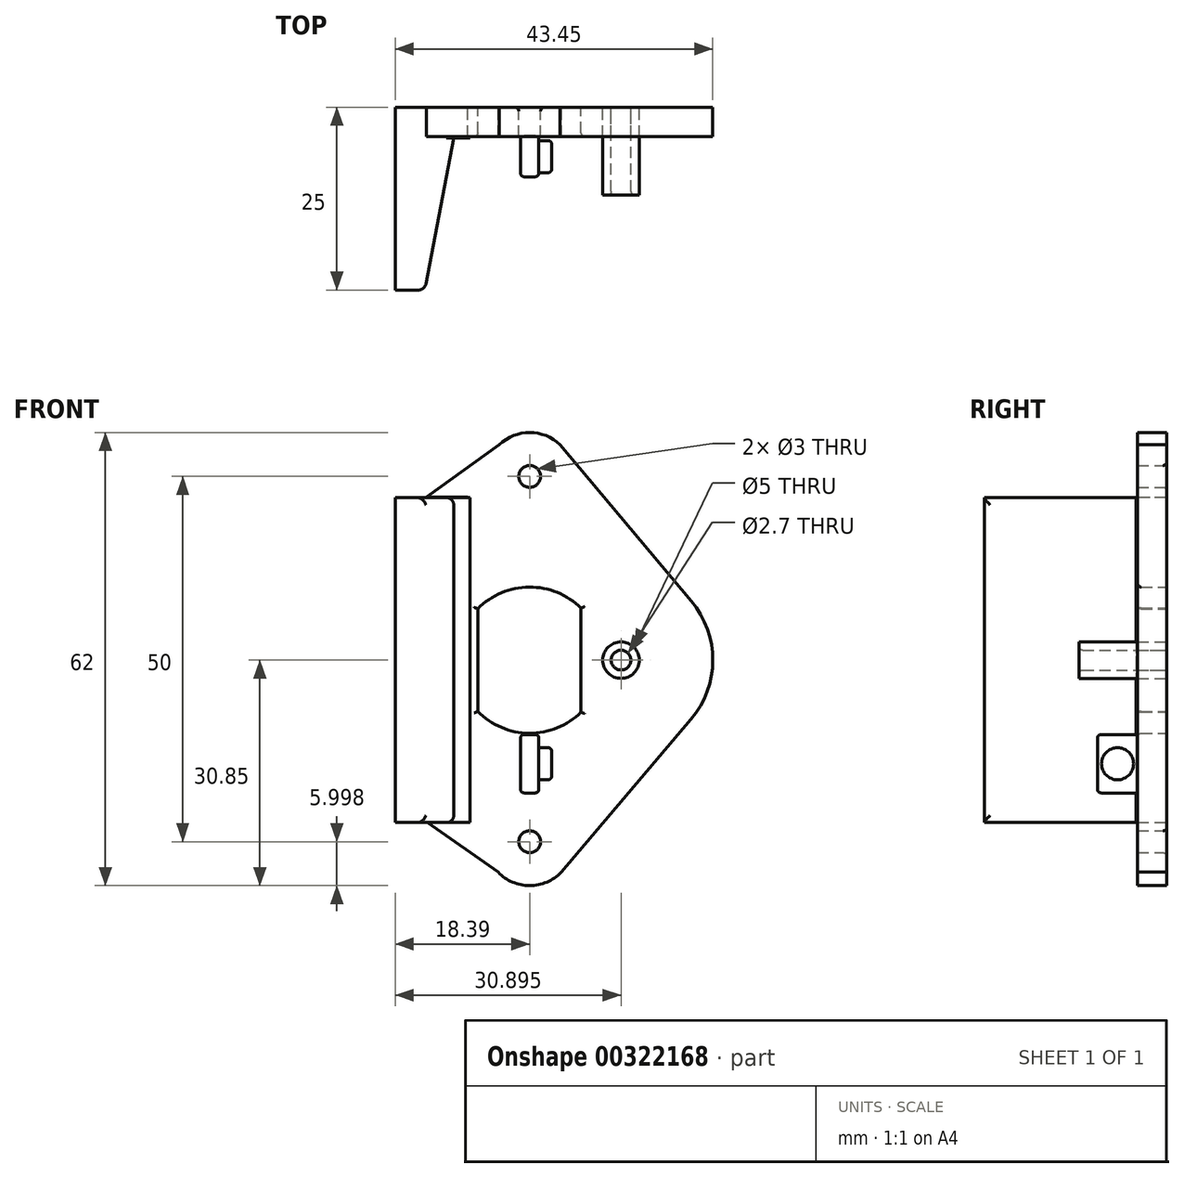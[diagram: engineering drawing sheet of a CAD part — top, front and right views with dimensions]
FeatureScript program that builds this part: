
annotation { "Feature Type Name" : "Feature", "Feature Type Description" : "" }
export const myFeature = defineFeature(function(context is Context, id is Id, definition is map)
    precondition{}
    {
        {
            var Q0;
            Q0=qCreatedBy(makeId("Front.planeOp"),FACE);
            var sketch = newSketch(context, id + "F0", { "sketchPlane" : qUnion([Q0])});
            skCircle(sketch, "E0", {"center": v(0, 25.15) * mm, "radius": 2.5 * mm});
            skCircle(sketch, "E1", {"center": v(0, -24.85) * mm, "radius": 2.5 * mm});
            skCircle(sketch, "E2", {"center": v(0, 25.15) * mm, "radius": 1.5 * mm});
            skCircle(sketch, "E3", {"center": v(0, -24.85) * mm, "radius": 1.5 * mm});
            skCircle(sketch, "E4", {"center": v(12.5, 0) * mm, "radius": 2.5 * mm});
            skLineSegment(sketch, "E5", {"start": v(-7.12, 7.03) * mm, "end": v(-7.12, -7.03) * mm});
            skLineSegment(sketch, "E6", {"start": v(7.03, -7.12) * mm, "end": v(7.03, 7.12) * mm});
            skLineSegment(sketch, "E7", {"start": v(1.25, -10.17) * mm, "end": v(-1.25, -10.17) * mm});
            skLineSegment(sketch, "E8", {"start": v(-1.25, -10.17) * mm, "end": v(-1.25, -18.17) * mm});
            skLineSegment(sketch, "E9", {"start": v(-1.25, -18.17) * mm, "end": v(1.25, -18.17) * mm});
            skLineSegment(sketch, "E10", {"start": v(1.25, -10.17) * mm, "end": v(1.25, -18.17) * mm});
            skLineSegment(sketch, "E11", {"start": v(-2.5, -14.17) * mm, "end": v(13.88, -14.2) * mm, "construction": true});
            skLineSegment(sketch, "E12", {"start": v(4.25, -16.38) * mm, "end": v(1.25, -16.38) * mm});
            skLineSegment(sketch, "E13", {"start": v(4.25, -16.38) * mm, "end": v(4.25, -11.98) * mm});
            skLineSegment(sketch, "E14", {"start": v(4.25, -11.98) * mm, "end": v(1.25, -11.98) * mm});
            skArc(sketch, "E15", {"start": v(-7.12, 7.03) * mm, "mid": v(-0.06, 10) * mm, "end": v(7.03, 7.12) * mm});
            skArc(sketch, "E16", {"start": v(7.03, -7.12) * mm, "mid": v(-0.06, -10) * mm, "end": v(-7.12, -7.03) * mm});
            skArc(sketch, "E17", {"start": v(-4.17, 29.46) * mm, "mid": v(0, 31.15) * mm, "end": v(4.17, 29.46) * mm});
            skArc(sketch, "E18", {"start": v(-4.32, -29.02) * mm, "mid": v(0, -30.85) * mm, "end": v(4.32, -29.02) * mm});
            skCircle(sketch, "E19", {"center": v(12.5, 0) * mm, "radius": 1.35 * mm});
            skLineSegment(sketch, "E20", {"start": v(4.17, 29.46) * mm, "end": v(22.12, 8.07) * mm});
            skLineSegment(sketch, "E21", {"start": v(4.32, -29.02) * mm, "end": v(22.07, -8.13) * mm});
            skArc(sketch, "E22", {"start": v(22.12, 8.07) * mm, "mid": v(25.06, -0.04) * mm, "end": v(22.07, -8.13) * mm});
            skLineSegment(sketch, "E23", {"start": v(-10.16, 22.33) * mm, "end": v(-10.16, -22.14) * mm});
            skLineSegment(sketch, "E24", {"start": v(-10.16, 22.33) * mm, "end": v(-14.16, 22.33) * mm});
            skLineSegment(sketch, "E25", {"start": v(-10.16, -22.14) * mm, "end": v(-14.16, -22.14) * mm});
            skLineSegment(sketch, "E26", {"start": v(-14.19, 22.33) * mm, "end": v(-18.19, 22.33) * mm});
            skLineSegment(sketch, "E27", {"start": v(-14.19, -22.14) * mm, "end": v(-18.19, -22.14) * mm});
            skLineSegment(sketch, "E28", {"start": v(-18.19, 22.33) * mm, "end": v(-18.19, -22.14) * mm});
            skLineSegment(sketch, "E29", {"start": v(-8.5, 22.33) * mm, "end": v(-8.5, -22.14) * mm});
            skLineSegment(sketch, "E30", {"start": v(-8.5, -22.14) * mm, "end": v(-10.16, -22.14) * mm});
            skLineSegment(sketch, "E31", {"start": v(-8.5, 22.33) * mm, "end": v(-10.16, 22.33) * mm});
            skLineSegment(sketch, "E32", {"start": v(-14.16, 22.33) * mm, "end": v(-14.16, -22.14) * mm});
            skLineSegment(sketch, "E33", {"start": v(-4.17, 29.46) * mm, "end": v(-14.16, 22.33) * mm});
            skLineSegment(sketch, "E34", {"start": v(-4.32, -29.02) * mm, "end": v(-14.16, -22.14) * mm});
            skSolve(sketch);
        }
        {
            var Q0;
            Q0=qCreatedBy(makeId("Right.planeOp"),FACE);
            var sketch = newSketch(context, id + "F1", { "sketchPlane" : qUnion([Q0])});
            skLineSegment(sketch, "E35", {"start": v(0, -14.18) * mm, "end": v(-22.56, -14.18) * mm, "construction": true});
            skLineSegment(sketch, "E36", {"start": v(0, -11.97) * mm, "end": v(-22.65, -11.97) * mm, "construction": true});
            skLineSegment(sketch, "E37", {"start": v(0, -16.36) * mm, "end": v(-22.55, -16.36) * mm, "construction": true});
            skLineSegment(sketch, "E38", {"start": v(-9.5, -18.19) * mm, "end": v(-9.5, -10.18) * mm});
            skLineSegment(sketch, "E39", {"start": v(0, -10.18) * mm, "end": v(0, -18.19) * mm});
            skCircle(sketch, "E40", {"center": v(-6.75, -14.18) * mm, "radius": 2.2 * mm});
            skLineSegment(sketch, "E41", {"start": v(-4, -10.18) * mm, "end": v(-4, -6.8) * mm, "construction": true});
            skLineSegment(sketch, "E42", {"start": v(-4, -6.8) * mm, "end": v(-4, -23.93) * mm, "construction": true});
            skLineSegment(sketch, "E43", {"start": v(-4, -10.18) * mm, "end": v(-4, -18.19) * mm});
            skLineSegment(sketch, "E44", {"start": v(-9.5, -10.18) * mm, "end": v(-4, -10.18) * mm});
            skLineSegment(sketch, "E45", {"start": v(-4, -18.19) * mm, "end": v(-9.5, -18.19) * mm});
            skLineSegment(sketch, "E46", {"start": v(0, 1.92) * mm, "end": v(-8, 1.92) * mm, "construction": true});
            skLineSegment(sketch, "E47", {"start": v(0, -1.88) * mm, "end": v(-8, -1.88) * mm, "construction": true});
            skLineSegment(sketch, "E48", {"start": v(-8, 1.92) * mm, "end": v(-8, -1.88) * mm, "construction": true});
            skLineSegment(sketch, "E49", {"start": v(-0.05, 17.6) * mm, "end": v(-25.05, 17.6) * mm, "construction": true});
            skLineSegment(sketch, "E50", {"start": v(-0.05, -17.49) * mm, "end": v(-24.94, -17.49) * mm, "construction": true});
            skLineSegment(sketch, "E51", {"start": v(-25.05, 17.6) * mm, "end": v(-24.94, -17.49) * mm, "construction": true});
            skLineSegment(sketch, "E52", {"start": v(0, 0) * mm, "end": v(-25.05, 17.6) * mm, "construction": true});
            skLineSegment(sketch, "E53", {"start": v(0, 0) * mm, "end": v(-24.94, -17.49) * mm, "construction": true});
            skLineSegment(sketch, "E54", {"start": v(-25, 0) * mm, "end": v(-0.05, -17.49) * mm, "construction": true});
            skLineSegment(sketch, "E55", {"start": v(-0.05, 17.6) * mm, "end": v(-25, 0) * mm, "construction": true});
            skCircle(sketch, "E56", {"center": v(-16.92, 8.8) * mm, "radius": 2.5 * mm});
            skCircle(sketch, "E57", {"center": v(-16.9, -8.76) * mm, "radius": 2.5 * mm});
            skCircle(sketch, "E58", {"center": v(-7.5, 4.92) * mm, "radius": 2.5 * mm});
            skSolve(sketch);
        }
        {
            var Q0;
            Q0=makeQuery(id+"F0.imprint","IMPRINT",FACE,{"disambiguationData":[TD([[makeQuery(id+"F0.imprint","IMPRINT",EDGE,{"derivedFrom":sQuery(id+"F0.wireOp",EDGE,"E0")}),-1.0]])]});
            var Q1;
            {var subQ0=sQuery(id+"F0.wireOp",EDGE,"E12");Q1=makeQuery(id+"F0.imprint","IMPRINT",FACE,{"disambiguationData":[TD([[makeQuery(id+"F0.imprint","IMPRINT",EDGE,{"derivedFrom":subQ0}),-1.0]])]});}
            var Q2;
            Q2=makeQuery(id+"F0.imprint","IMPRINT",FACE,{"disambiguationData":[TD([[makeQuery(id+"F0.imprint","IMPRINT",EDGE,{"derivedFrom":sQuery(id+"F0.wireOp",EDGE,"E19")}),1.0]])]});
            extrude(context, id + "F2", {"entities" : qUnion([Q0, Q1, Q2]), "depth" : 4 * mm});
        }
        {
            var Q0;
            {var subQ1=sQuery(id+"F0.wireOp",EDGE,"E7");Q0=makeQuery(id+"F0.imprint","IMPRINT",FACE,{"disambiguationData":[TD([[makeQuery(id+"F0.imprint","IMPRINT",EDGE,{"derivedFrom":subQ1}),1.0]])]});}
            extrude(context, id + "F3", {"entities" : qUnion([Q0]), "operationType" : NewBodyOperationType.ADD, "depth" : 9.5 * mm});
        }
        {
            var Q0;
            Q0=makeQuery(id+"F1.imprint","IMPRINT",FACE,{"disambiguationData":[TD([[makeQuery(id+"F1.imprint","IMPRINT",EDGE,{"derivedFrom":sQuery(id+"F1.wireOp",EDGE,"E40")}),1.0]])]});
            extrude(context, id + "F4", {"entities" : qUnion([Q0]), "operationType" : NewBodyOperationType.ADD, "depth" : 3 * mm});
        }
        {
            var Q0;
            Q0=makeQuery(id+"F0.imprint","IMPRINT",FACE,{"disambiguationData":[TD([[makeQuery(id+"F0.imprint","IMPRINT",EDGE,{"derivedFrom":sQuery(id+"F0.wireOp",EDGE,"E4")}),1.0]])]});
            extrude(context, id + "F5", {"entities" : qUnion([Q0]), "depth" : 12 * mm});
        }
        {
            var Q0;
            Q0=makeQuery(id+"F0.imprint","IMPRINT",FACE,{"disambiguationData":[TD([[makeQuery(id+"F0.imprint","IMPRINT",EDGE,{"derivedFrom":sQuery(id+"F0.wireOp",EDGE,"E0")}),1.0]])]});
            var Q1;
            Q1=makeQuery(id+"F0.imprint","IMPRINT",FACE,{"disambiguationData":[TD([[makeQuery(id+"F0.imprint","IMPRINT",EDGE,{"derivedFrom":sQuery(id+"F0.wireOp",EDGE,"E1")}),1.0]])]});
            extrude(context, id + "F6", {"entities" : qUnion([Q0, Q1]), "operationType" : NewBodyOperationType.ADD, "depth" : 4 * mm});
        }
        {
            var Q0;
            Q0=makeQuery(id+"F2.opExtrude","CAP_EDGE",EDGE,{"disambiguationData":[OSD([sQuery(id+"F0.wireOp",EDGE,"E15")])],"isStart":false});
            var Q1;
            Q1=makeQuery(id+"F2.opExtrude","CAP_EDGE",EDGE,{"disambiguationData":[OSD([sQuery(id+"F0.wireOp",EDGE,"E5")])],"isStart":false});
            var Q2;
            Q2=makeQuery(id+"F2.opExtrude","CAP_EDGE",EDGE,{"disambiguationData":[OSD([sQuery(id+"F0.wireOp",EDGE,"E6")])],"isStart":false});
            var Q3;
            Q3=makeQuery(id+"F2.opExtrude","CAP_EDGE",EDGE,{"disambiguationData":[OSD([sQuery(id+"F0.wireOp",EDGE,"E16")])],"isStart":false});
            fillet(context, id + "F7", {"entities" : qUnion([Q0, Q1, Q2, Q3]), "radius" : 0.5 * mm, "tangentPropagation" : true, "allowEdgeOverflow" : false});
        }
        {
            var Q0;
            Q0=makeQuery(id+"F5.opExtrude","CAP_EDGE",EDGE,{"disambiguationData":[OSD([sQuery(id+"F0.wireOp",EDGE,"E19")])],"isStart":false});
            var Q1;
            Q1=makeQuery(id+"F6.opExtrude","CAP_EDGE",EDGE,{"disambiguationData":[OSD([sQuery(id+"F0.wireOp",EDGE,"E3")])],"isStart":true});
            var Q2;
            Q2=makeQuery(id+"F6.opExtrude","CAP_EDGE",EDGE,{"disambiguationData":[OSD([sQuery(id+"F0.wireOp",EDGE,"E2")])],"isStart":true});
            fillet(context, id + "F8", {"entities" : qUnion([Q0, Q1, Q2]), "radius" : 0.5 * mm, "tangentPropagation" : true, "allowEdgeOverflow" : false});
        }
        {
            var Q0;
            Q0=makeQuery(id+"F3.opExtrude","SWEPT_EDGE",EDGE,{"disambiguationData":[OSD([sQuery(id+"F0.wireOp",EDGE,"E7"),sQuery(id+"F0.wireOp",EDGE,"E10")])]});
            var Q1;
            Q1=makeQuery(id+"F3.opExtrude","SWEPT_EDGE",EDGE,{"disambiguationData":[OSD([sQuery(id+"F0.wireOp",EDGE,"E9"),sQuery(id+"F0.wireOp",EDGE,"E10")])]});
            var Q2;
            Q2=makeQuery(id+"F3.opExtrude","CAP_EDGE",EDGE,{"disambiguationData":[OSD([sQuery(id+"F0.wireOp",EDGE,"E10")])],"isStart":false});
            var Q3;
            Q3=makeQuery(id+"F3.opExtrude","CAP_EDGE",EDGE,{"disambiguationData":[OSD([sQuery(id+"F0.wireOp",EDGE,"E8")])],"isStart":false});
            var Q4;
            Q4=makeQuery(id+"F3.opExtrude","SWEPT_EDGE",EDGE,{"disambiguationData":[OSD([sQuery(id+"F0.wireOp",EDGE,"E7"),sQuery(id+"F0.wireOp",EDGE,"E8")])]});
            var Q5;
            Q5=makeQuery(id+"F3.opExtrude","SWEPT_EDGE",EDGE,{"disambiguationData":[OSD([sQuery(id+"F0.wireOp",EDGE,"E8"),sQuery(id+"F0.wireOp",EDGE,"E9")])]});
            var Q6;
            Q6=makeQuery(id+"F3.opExtrude","CAP_EDGE",EDGE,{"disambiguationData":[OSD([sQuery(id+"F0.wireOp",EDGE,"E7")])],"isStart":false});
            var Q7;
            Q7=makeQuery(id+"F3.opExtrude","CAP_EDGE",EDGE,{"disambiguationData":[OSD([sQuery(id+"F0.wireOp",EDGE,"E9")])],"isStart":false});
            fillet(context, id + "F9", {"entities" : qUnion([Q0, Q1, Q2, Q3, Q4, Q5, Q6, Q7]), "radius" : 0.5 * mm, "tangentPropagation" : true, "allowEdgeOverflow" : false});
        }
        {
            var Q0;
            Q0=makeQuery(id+"F4.opExtrude","CAP_EDGE",EDGE,{"disambiguationData":[OSD([sQuery(id+"F1.wireOp",EDGE,"E40")])],"isStart":false});
            fillet(context, id + "F10", {"entities" : qUnion([Q0]), "radius" : 0.5 * mm, "tangentPropagation" : true, "allowEdgeOverflow" : false});
        }
        {
            var Q0;
            Q0=qCreatedBy(makeId("Top.planeOp"),FACE);
            var sketch = newSketch(context, id + "F11", { "sketchPlane" : qUnion([Q0])});
            skLineSegment(sketch, "E59", {"start": v(-18.39, 0) * mm, "end": v(-18.39, -52.37) * mm, "construction": true});
            skLineSegment(sketch, "E60", {"start": v(-18.39, -52.37) * mm, "end": v(15, -52.37) * mm, "construction": true});
            skLineSegment(sketch, "E61", {"start": v(-14.4, 0) * mm, "end": v(-14.4, -52.37) * mm, "construction": true});
            skLineSegment(sketch, "E62", {"start": v(-8.2, 0) * mm, "end": v(-8.2, -52.37) * mm, "construction": true});
            skLineSegment(sketch, "E63", {"start": v(-10.4, 0) * mm, "end": v(-10.4, -52.37) * mm, "construction": true});
            skLineSegment(sketch, "E64", {"start": v(32.18, -25) * mm, "end": v(-36.58, -25) * mm, "construction": true});
            skLineSegment(sketch, "E65", {"start": v(-10.4, -4.2) * mm, "end": v(-14.4, -25) * mm});
            skLineSegment(sketch, "E66", {"start": v(-14.4, -25) * mm, "end": v(-18.39, -25) * mm});
            skLineSegment(sketch, "E67", {"start": v(-18.39, -25) * mm, "end": v(-18.39, 0) * mm});
            skLineSegment(sketch, "E68", {"start": v(-8.2, -4.2) * mm, "end": v(-11.64, -10.67) * mm});
            skLineSegment(sketch, "E69", {"start": v(-11.64, -10.67) * mm, "end": v(-8.2, -4.2) * mm});
            skLineSegment(sketch, "E70", {"start": v(-10.4, -4.2) * mm, "end": v(-10.4, 0) * mm});
            skLineSegment(sketch, "E71", {"start": v(-10.4, 0) * mm, "end": v(-18.39, 0) * mm});
            skLineSegment(sketch, "E72", {"start": v(-8.2, -4.2) * mm, "end": v(-10.4, -4.2) * mm});
            skLineSegment(sketch, "E73", {"start": v(-8.2, -4.2) * mm, "end": v(-8.2, 0) * mm});
            skLineSegment(sketch, "E74", {"start": v(-14.4, 0) * mm, "end": v(-8.2, 0) * mm});
            skSolve(sketch);
        }
        {
            var Q0;
            {var subQ2=sQuery(id+"F11.wireOp",EDGE,"E69");Q0=makeQuery(id+"F11.imprint","IMPRINT",FACE,{"disambiguationData":[TD([[makeQuery(id+"F11.imprint","IMPRINT",EDGE,{"derivedFrom":subQ2}),1.0]])]});}
            var Q1;
            {var subQ0=sQuery(id+"F11.wireOp",EDGE,"E66");Q1=makeQuery(id+"F11.imprint","IMPRINT",FACE,{"disambiguationData":[TD([[makeQuery(id+"F11.imprint","IMPRINT",EDGE,{"derivedFrom":subQ0}),-1.0]])]});}
            var Q2;
            {var subQ0=sQuery(id+"F11.wireOp",EDGE,"E70");Q2=makeQuery(id+"F11.imprint","IMPRINT",FACE,{"disambiguationData":[TD([[makeQuery(id+"F11.imprint","IMPRINT",EDGE,{"derivedFrom":subQ0}),-1.0]])]});}
            extrude(context, id + "F12", {"entities" : qUnion([Q0, Q1, Q2]), "operationType" : NewBodyOperationType.ADD, "endBound" : BoundingType.SYMMETRIC, "depth" : 44.47 * mm});
        }
        {
            var Q0;
            Q0=sQuery(id+"F1.wireOp",VERTEX,"E56.center");
            var Q1;
            Q1=sQuery(id+"F1.wireOp",VERTEX,"E57.center");
            var Q2;
            Q2=makeQuery(id+"F5.opExtrude","SWEPT_BODY",BODY,{"disambiguationData":[OSD([sQuery(id+"F0.wireOp",EDGE,"E4"),sQuery(id+"F0.wireOp",EDGE,"E19")])]});
            hole(context, id + "F13", {"style" : HoleStyle.C_BORE, "endStyle" : HoleEndStyle.THROUGH, "holeDiameter" : 5 * mm, "cBoreDiameter" : 10 * mm, "cBoreDepth" : 0.2 * mm, "tappedDepth" : 12 * mm, "tapClearance" : 3, "locations" : qUnion([Q0, Q1]), "scope" : qUnion([Q2])});
        }
        {
            var Q0;
            Q0=sQuery(id+"F1.wireOp",VERTEX,"E58.center");
            var Q1;
            Q1=makeQuery(id+"F5.opExtrude","SWEPT_BODY",BODY,{"disambiguationData":[OSD([sQuery(id+"F0.wireOp",EDGE,"E4"),sQuery(id+"F0.wireOp",EDGE,"E19")])]});
            hole(context, id + "F14", {"style" : HoleStyle.SIMPLE, "endStyle" : HoleEndStyle.THROUGH, "holeDiameter" : 8.7 * mm, "tappedDepth" : 12 * mm, "tapClearance" : 3, "locations" : qUnion([Q0]), "scope" : qUnion([Q1])});
        }
        {
            var Q0;
            Q0=makeQuery(id+"F12.opExtrude","CAP_EDGE",EDGE,{"disambiguationData":[OSD([sQuery(id+"F11.wireOp",EDGE,"E65")])],"isStart":true});
            var Q1;
            Q1=makeQuery(id+"F12.opExtrude","CAP_EDGE",EDGE,{"disambiguationData":[OSD([sQuery(id+"F11.wireOp",EDGE,"E69")])],"isStart":true});
            var Q2;
            Q2=makeQuery(id+"F12.opExtrude","SWEPT_EDGE",EDGE,{"disambiguationData":[OSD([sQuery(id+"F11.wireOp",EDGE,"E65"),sQuery(id+"F11.wireOp",EDGE,"E66")])]});
            var Q3;
            Q3=makeQuery(id+"F12.opExtrude","CAP_EDGE",EDGE,{"disambiguationData":[OSD([sQuery(id+"F11.wireOp",EDGE,"E65")])],"isStart":false});
            var Q4;
            Q4=makeQuery(id+"F12.opExtrude","CAP_EDGE",EDGE,{"disambiguationData":[OSD([sQuery(id+"F11.wireOp",EDGE,"E69")])],"isStart":false});
            fillet(context, id + "F15", {"entities" : qUnion([Q0, Q1, Q2, Q3, Q4]), "radius" : 1 * mm, "tangentPropagation" : true, "allowEdgeOverflow" : false});
        }
    });
